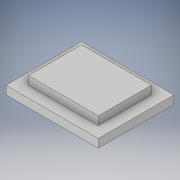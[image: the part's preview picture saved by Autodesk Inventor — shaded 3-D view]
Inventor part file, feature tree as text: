
AUTODESK INVENTOR PART (.ipt)
format: ipt  version: 2019 (Build 230136000, 136)  size: 107,008 bytes
history: native  units: mm
features: extrude x2, sketch x2
ambient origin geometry x8: Origin, YZ Plane, XZ Plane, XY Plane, X Axis, Y Axis, Z Axis, Center Point
bodies: Solid1 (feature_tree)
feature tree (4):
  extrude  "Extrusion1"  Depth=13.5mm
  extrude  "Extrusion2"  Depth=2.0mm
  sketch  "Sketch1"  dims[d0=16.5mm d1=13.5mm]
  sketch  "Sketch2"  dims[d2=1.5mm d3=0.0mm d4=2.0mm d5=2.0mm d6=1.5mm d7=0.0mm]
